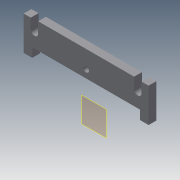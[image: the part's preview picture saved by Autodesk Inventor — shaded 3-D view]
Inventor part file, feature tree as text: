
AUTODESK INVENTOR PART (.ipt)
format: ipt  version: 2014 SP1 (Build 180222100, 222)  size: 101,888 bytes
history: native  units: in
note: dims shown in document units (in); Inventor stores cm internally (conversion verified against a paired STEP export)
features: plane x1, extrude x1, sketch x1
ambient origin geometry x8: Origin, YZ Plane, XZ Plane, XY Plane, X Axis, Y Axis, Z Axis, Center Point
bodies: Solid1 (feature_tree)
feature tree (3):
  plane  "Work Plane1"
  extrude  "Extrusion1"  Depth=1.1in
  sketch  "Sketch1"  dims[d0=5.5in d1=2.75in d2=1.25in d3=1.5in d4=0.3409in d5=0.0in d6=0.325in d9=1.025in d10=0.475in d12=0.4in d15=4.75in d16=1.5in d17=2.375in d18=2.75in d19=1.225in d20=1.225in d22=0.25in d23=2.275in d24=1.1in]
